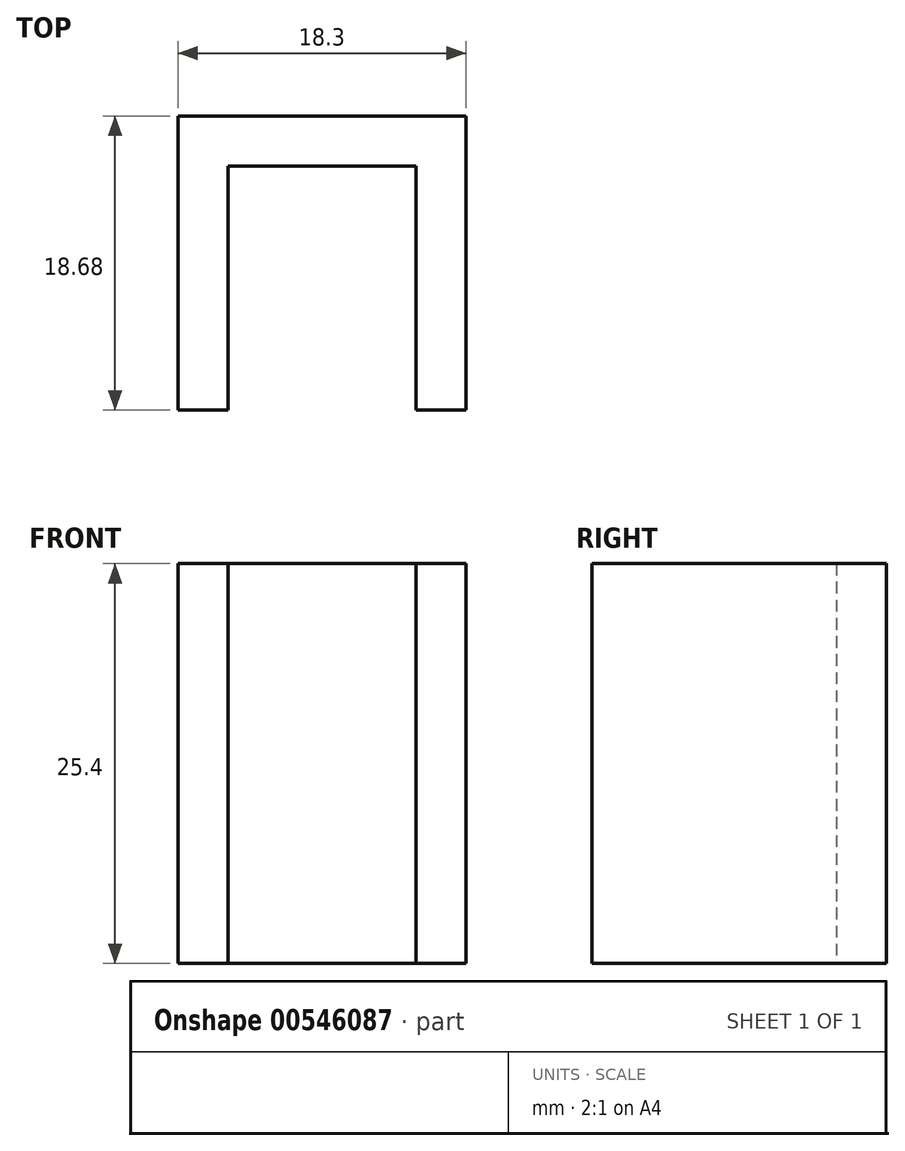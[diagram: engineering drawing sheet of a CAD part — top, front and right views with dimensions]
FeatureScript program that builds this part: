
annotation { "Feature Type Name" : "Feature", "Feature Type Description" : "" }
export const myFeature = defineFeature(function(context is Context, id is Id, definition is map)
    precondition{}
    {
        {
            var Q0;
            Q0=qCreatedBy(makeId("Top.planeOp"),FACE);
            var sketch = newSketch(context, id + "F0", { "sketchPlane" : qUnion([Q0])});
            skLineSegment(sketch, "E0.bottom", {"start": v(9.15, 9.34) * mm, "end": v(-9.15, 9.34) * mm});
            skLineSegment(sketch, "E0.top", {"start": v(9.15, -9.34) * mm, "end": v(5.98, -9.34) * mm});
            skLineSegment(sketch, "E0.left", {"start": v(9.15, 9.34) * mm, "end": v(9.15, -9.34) * mm});
            skLineSegment(sketch, "E0.right", {"start": v(-9.15, 9.34) * mm, "end": v(-9.15, -9.34) * mm});
            skPoint(sketch, "E0.middle", {"position": v(0, 0) * mm});
            skLineSegment(sketch, "E1.top", {"start": v(-5.98, 6.16) * mm, "end": v(5.98, 6.16) * mm});
            skLineSegment(sketch, "E1.left", {"start": v(-5.98, -9.34) * mm, "end": v(-5.98, 6.16) * mm});
            skLineSegment(sketch, "E1.right", {"start": v(5.98, -9.34) * mm, "end": v(5.98, 6.16) * mm});
            skLineSegment(sketch, "E2.trimOffspring", {"start": v(-5.98, -9.34) * mm, "end": v(-9.15, -9.34) * mm});
            skSolve(sketch);
        }
        {
            var Q0;
            Q0=makeQuery(id+"F0.imprint","IMPRINT",FACE,{"disambiguationData":[TD([[makeQuery(id+"F0.imprint","IMPRINT",EDGE,{"derivedFrom":sQuery(id+"F0.wireOp",EDGE,"E0.bottom")}),1.0]])]});
            extrude(context, id + "F1", {"entities" : qUnion([Q0]), "depth" : 25.4 * mm, "offsetDistance" : 25.4 * mm});
        }
    });
